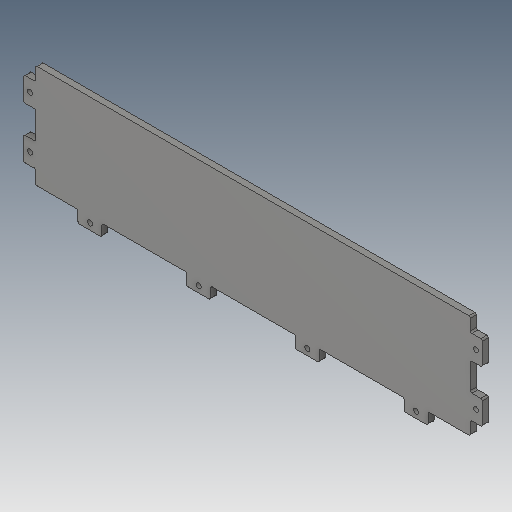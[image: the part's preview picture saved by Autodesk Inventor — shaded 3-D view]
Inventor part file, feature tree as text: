
AUTODESK INVENTOR PART (.ipt)
format: ipt  version: 2023.5 (Build 275446000, 446)  size: 145,920 bytes
history: native  units: in
note: dims shown in document units (in); Inventor stores cm internally (conversion verified against a paired STEP export)
features: mirror x1
ambient origin geometry x8: Origin, YZ Plane, XZ Plane, XY Plane, X Axis, Y Axis, Z Axis, Center Point
bodies: Solid1 (feature_tree)
feature tree (1):
  mirror  "Mirror2"
